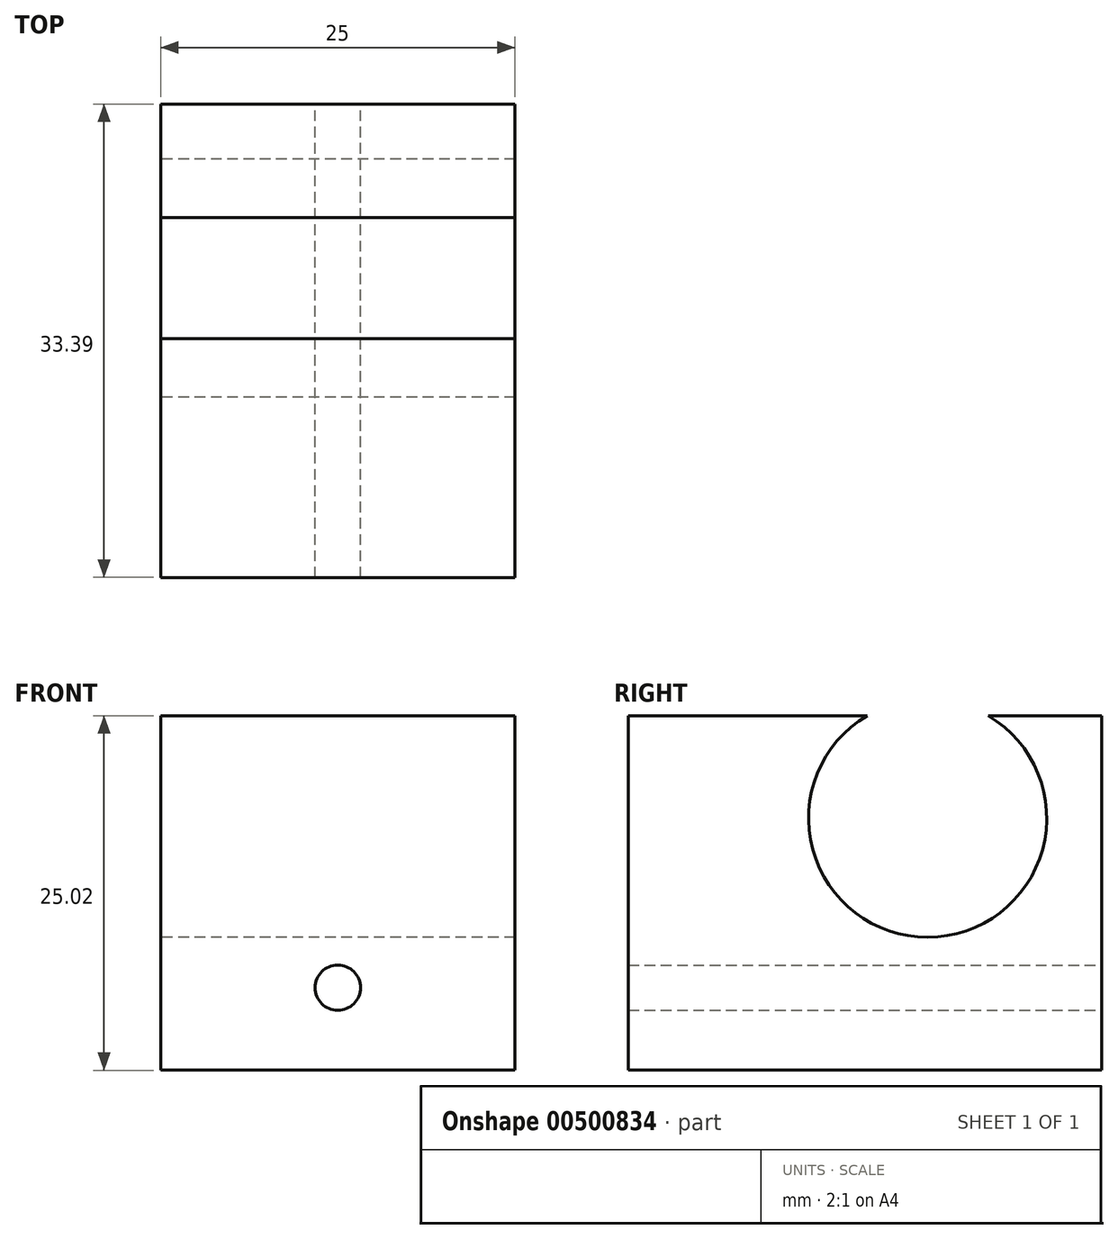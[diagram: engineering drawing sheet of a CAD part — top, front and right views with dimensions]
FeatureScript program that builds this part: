
annotation { "Feature Type Name" : "Feature", "Feature Type Description" : "" }
export const myFeature = defineFeature(function(context is Context, id is Id, definition is map)
    precondition{}
    {
        {
            var Q0;
            Q0=qCreatedBy(makeId("Right.planeOp"),FACE);
            var sketch = newSketch(context, id + "F0", { "sketchPlane" : qUnion([Q0])});
            skArc(sketch, "E0", {"start": v(-4.42, 17.09) * mm, "mid": v(-0.15, 1.46) * mm, "end": v(4.12, 17.1) * mm});
            skPoint(sketch, "E1", {"position": v(-0.13, 8.75) * mm});
            skLineSegment(sketch, "E2", {"start": v(-0.13, 8.75) * mm, "end": v(6.8, 8.75) * mm, "construction": true});
            skLineSegment(sketch, "E3", {"start": v(-0.13, 8.75) * mm, "end": v(-0.13, 5.5) * mm, "construction": true});
            skLineSegment(sketch, "E4", {"start": v(12.12, 17.07) * mm, "end": v(12.12, -7.93) * mm});
            skLineSegment(sketch, "E5", {"start": v(4.12, 17.1) * mm, "end": v(12.12, 17.07) * mm});
            skLineSegment(sketch, "E6", {"start": v(12.12, -7.93) * mm, "end": v(-21.27, -7.93) * mm});
            skLineSegment(sketch, "E7", {"start": v(-21.27, 17.07) * mm, "end": v(-21.27, -7.93) * mm});
            skLineSegment(sketch, "E8", {"start": v(-21.27, 17.07) * mm, "end": v(-4.42, 17.09) * mm});
            skSolve(sketch);
        }
        {
            var Q0;
            Q0 = qSketchRegion(id + "F0", true);
            extrude(context, id + "F1", {"entities" : qUnion([Q0]), "depth" : 25 * mm, "offsetDistance" : 25 * mm});
        }
        {
            var Q0;
            Q0=makeQuery(id+"F1.opExtrude","SWEPT_FACE",FACE,{"disambiguationData":[OSD([sQuery(id+"F0.wireOp",EDGE,"E4")])]});
            var sketch = newSketch(context, id + "F2", { "sketchPlane" : qUnion([Q0])});
            skLineSegment(sketch, "E9", {"start": v(-25, -2.1) * mm, "end": v(0, -2.1) * mm, "construction": true});
            skLineSegment(sketch, "E10", {"start": v(-12.5, 14.97) * mm, "end": v(-12.5, -5.03) * mm, "construction": true});
            skCircle(sketch, "E11", {"center": v(-12.5, -2.1) * mm, "radius": 1.6 * mm});
            skSolve(sketch);
        }
        {
            var Q0;
            Q0 = qSketchRegion(id + "F2", true);
            extrude(context, id + "F3", {"entities" : qUnion([Q0]), "operationType" : NewBodyOperationType.REMOVE, "oppositeDirection" : true, "depth" : 39.6 * mm, "offsetDistance" : 25 * mm});
        }
    });
